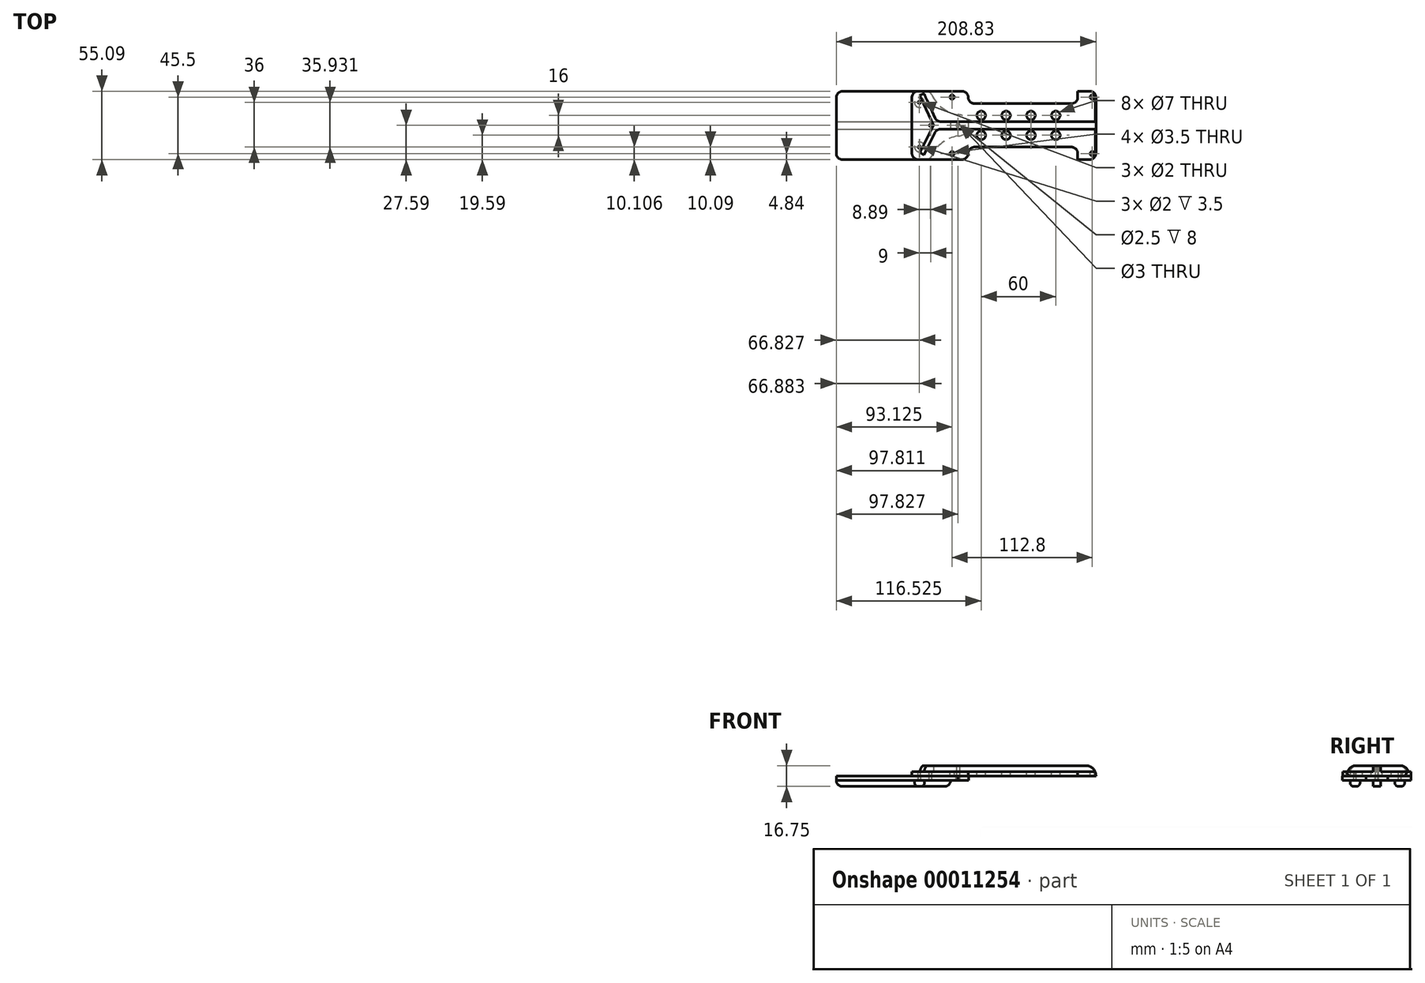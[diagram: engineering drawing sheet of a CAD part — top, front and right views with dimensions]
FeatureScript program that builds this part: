
annotation { "Feature Type Name" : "Feature", "Feature Type Description" : "" }
export const myFeature = defineFeature(function(context is Context, id is Id, definition is map)
    precondition{}
    {
        {
            var Q0;
            Q0=qCreatedBy(makeId("Front.planeOp"),FACE);
            var sketch = newSketch(context, id + "F0", { "sketchPlane" : qUnion([Q0])});
            skLineSegment(sketch, "E0.bottom", {"start": v(-74.3, 0) * mm, "end": v(73.7, 0) * mm});
            skLineSegment(sketch, "E0.top", {"start": v(-74.3, 3.25) * mm, "end": v(73.7, 3.25) * mm});
            skLineSegment(sketch, "E0.left", {"start": v(-74.3, 0) * mm, "end": v(-74.3, 3.25) * mm});
            skLineSegment(sketch, "E0.right", {"start": v(73.7, 0) * mm, "end": v(73.7, 3.25) * mm});
            skSolve(sketch);
        }
        {
            var Q0;
            Q0 = qSketchRegion(id + "F0", true);
            extrude(context, id + "F1", {"entities" : qUnion([Q0]), "endBound" : BoundingType.SYMMETRIC, "oppositeDirection" : true, "depth" : (55) * mm});
        }
        {
            var Q0;
            Q0=makeQuery(id+"F1.opExtrude","SWEPT_FACE",FACE,{"disambiguationData":[OSD([sQuery(id+"F0.wireOp",EDGE,"E0.top")])]});
            var sketch = newSketch(context, id + "F2", { "sketchPlane" : qUnion([Q0])});
            skCircle(sketch, "E1", {"center": v(70.8, 22.75) * mm, "radius": 1.75 * mm});
            skCircle(sketch, "E2", {"center": v(70.8, -22.75) * mm, "radius": 1.75 * mm});
            skCircle(sketch, "E3", {"center": v(-42, 22.75) * mm, "radius": 1.75 * mm});
            skCircle(sketch, "E4", {"center": v(-42, -22.75) * mm, "radius": 1.75 * mm});
            skLineSegment(sketch, "E5.bottom", {"start": v(-29, 27.5) * mm, "end": v(59, 27.5) * mm});
            skLineSegment(sketch, "E5.top", {"start": v(-29, 17.5) * mm, "end": v(59, 17.5) * mm});
            skLineSegment(sketch, "E5.left", {"start": v(-29, 27.5) * mm, "end": v(-29, 17.5) * mm});
            skLineSegment(sketch, "E5.right", {"start": v(59, 27.5) * mm, "end": v(59, 17.5) * mm});
            skLineSegment(sketch, "E6.bottom", {"start": v(-29, -27.5) * mm, "end": v(59, -27.5) * mm});
            skLineSegment(sketch, "E6.top", {"start": v(-29, -17.5) * mm, "end": v(59, -17.5) * mm});
            skLineSegment(sketch, "E6.left", {"start": v(-29, -27.5) * mm, "end": v(-29, -17.5) * mm});
            skLineSegment(sketch, "E6.right", {"start": v(59, -27.5) * mm, "end": v(59, -17.5) * mm});
            skCircle(sketch, "E7", {"center": v(-18.6, 8) * mm, "radius": 3.5 * mm});
            skCircle(sketch, "E8", {"center": v(1.4, 8) * mm, "radius": 3.5 * mm});
            skCircle(sketch, "E9", {"center": v(21.4, 8) * mm, "radius": 3.5 * mm});
            skCircle(sketch, "E10", {"center": v(41.4, 8) * mm, "radius": 3.5 * mm});
            skCircle(sketch, "E11", {"center": v(41.4, -8) * mm, "radius": 3.5 * mm});
            skCircle(sketch, "E12", {"center": v(21.4, -8) * mm, "radius": 3.5 * mm});
            skCircle(sketch, "E13", {"center": v(1.4, -8) * mm, "radius": 3.5 * mm});
            skCircle(sketch, "E14", {"center": v(-18.6, -8) * mm, "radius": 3.5 * mm});
            skCircle(sketch, "E15", {"center": v(-68.3, 18.5) * mm, "radius": 1 * mm});
            skCircle(sketch, "E16", {"center": v(-68.3, -17.5) * mm, "radius": 1 * mm});
            skCircle(sketch, "E17", {"center": v(-59.3, 0) * mm, "radius": 1 * mm});
            skSolve(sketch);
        }
        {
            var Q0;
            Q0 = qSketchRegion(id + "F2", true);
            extrude(context, id + "F3", {"entities" : qUnion([Q0]), "operationType" : NewBodyOperationType.REMOVE, "endBound" : BoundingType.THROUGH_ALL, "oppositeDirection" : true, "depth" : 25 * mm});
        }
        {
            var Q0;
            Q0=makeQuery(id+"F3.boolean.opBoolean","COPY",EDGE,{"derivedFrom":makeQuery(id+"F3.opExtrude","SWEPT_EDGE",EDGE,{"disambiguationData":[OSD([sQuery(id+"F0.wireOp",EDGE,"E0.top"),sQuery(id+"F2.wireOp",EDGE,"E6.bottom"),sQuery(id+"F2.wireOp",EDGE,"E6.right")])]})});
            var Q1;
            Q1=makeQuery(id+"F3.boolean.opBoolean","COPY",EDGE,{"derivedFrom":makeQuery(id+"F3.opExtrude","SWEPT_EDGE",EDGE,{"disambiguationData":[OSD([sQuery(id+"F2.wireOp",EDGE,"E6.top"),sQuery(id+"F2.wireOp",EDGE,"E6.right")])]})});
            var Q2;
            Q2=makeQuery(id+"F3.boolean.opBoolean","COPY",EDGE,{"derivedFrom":makeQuery(id+"F3.opExtrude","SWEPT_EDGE",EDGE,{"disambiguationData":[OSD([sQuery(id+"F0.wireOp",EDGE,"E0.top"),sQuery(id+"F2.wireOp",EDGE,"E6.bottom"),sQuery(id+"F2.wireOp",EDGE,"E6.left")])]})});
            var Q3;
            Q3=makeQuery(id+"F3.boolean.opBoolean","COPY",EDGE,{"derivedFrom":makeQuery(id+"F3.opExtrude","SWEPT_EDGE",EDGE,{"disambiguationData":[OSD([sQuery(id+"F0.wireOp",EDGE,"E0.top"),sQuery(id+"F2.wireOp",EDGE,"E5.bottom"),sQuery(id+"F2.wireOp",EDGE,"E5.right")])]})});
            var Q4;
            Q4=makeQuery(id+"F3.boolean.opBoolean","COPY",EDGE,{"derivedFrom":makeQuery(id+"F3.opExtrude","SWEPT_EDGE",EDGE,{"disambiguationData":[OSD([sQuery(id+"F2.wireOp",EDGE,"E6.top"),sQuery(id+"F2.wireOp",EDGE,"E6.left")])]})});
            var Q5;
            Q5=makeQuery(id+"F3.boolean.opBoolean","COPY",EDGE,{"derivedFrom":makeQuery(id+"F3.opExtrude","SWEPT_EDGE",EDGE,{"disambiguationData":[OSD([sQuery(id+"F0.wireOp",EDGE,"E0.top"),sQuery(id+"F2.wireOp",EDGE,"E5.bottom"),sQuery(id+"F2.wireOp",EDGE,"E5.left")])]})});
            var Q6;
            Q6=makeQuery(id+"F3.boolean.opBoolean","COPY",EDGE,{"derivedFrom":makeQuery(id+"F3.opExtrude","SWEPT_EDGE",EDGE,{"disambiguationData":[OSD([sQuery(id+"F2.wireOp",EDGE,"E5.top"),sQuery(id+"F2.wireOp",EDGE,"E5.left")])]})});
            var Q7;
            Q7=makeQuery(id+"F3.boolean.opBoolean","COPY",EDGE,{"derivedFrom":makeQuery(id+"F3.opExtrude","SWEPT_EDGE",EDGE,{"disambiguationData":[OSD([sQuery(id+"F2.wireOp",EDGE,"E5.top"),sQuery(id+"F2.wireOp",EDGE,"E5.right")])]})});
            var Q8;
            Q8=makeQuery(id+"F1.opExtrude","CAP_EDGE",EDGE,{"disambiguationData":[OSD([sQuery(id+"F0.wireOp",EDGE,"E0.right")])],"isStart":false});
            var Q9;
            Q9=makeQuery(id+"F1.opExtrude","CAP_EDGE",EDGE,{"disambiguationData":[OSD([sQuery(id+"F0.wireOp",EDGE,"E0.right")])],"isStart":true});
            var Q10;
            Q10=makeQuery(id+"F1.opExtrude","CAP_EDGE",EDGE,{"disambiguationData":[OSD([sQuery(id+"F0.wireOp",EDGE,"E0.left")])],"isStart":false});
            var Q11;
            Q11=makeQuery(id+"F1.opExtrude","CAP_EDGE",EDGE,{"disambiguationData":[OSD([sQuery(id+"F0.wireOp",EDGE,"E0.left")])],"isStart":true});
            fillet(context, id + "F4", {"entities" : qUnion([Q0, Q1, Q2, Q3, Q4, Q5, Q6, Q7, Q8, Q9, Q10, Q11]), "radius" : 5 * mm, "tangentPropagation" : true, "allowEdgeOverflow" : false});
        }
        {
            var Q0;
            Q0=makeQuery(id+"F1.opExtrude","SWEPT_FACE",FACE,{"disambiguationData":[OSD([sQuery(id+"F0.wireOp",EDGE,"E0.top")])]});
            var sketch = newSketch(context, id + "F5", { "sketchPlane" : qUnion([Q0])});
            skLineSegment(sketch, "E18.bottom", {"start": v(-54.3, 3) * mm, "end": v(73.7, 3) * mm});
            skLineSegment(sketch, "E18.top", {"start": v(-54.3, -3) * mm, "end": v(73.7, -3) * mm});
            skLineSegment(sketch, "E18.left", {"start": v(-54.3, 3) * mm, "end": v(-54.3, -3) * mm});
            skLineSegment(sketch, "E18.right", {"start": v(73.7, 3) * mm, "end": v(73.7, -3) * mm});
            skSolve(sketch);
        }
        {
            var Q0;
            Q0 = qSketchRegion(id + "F5", true);
            extrude(context, id + "F6", {"entities" : qUnion([Q0]), "operationType" : NewBodyOperationType.ADD, "depth" : 5 * mm});
        }
        {
            var Q0;
            Q0=qCreatedBy(makeId("Top.planeOp"),FACE);
            var sketch = newSketch(context, id + "F7", { "sketchPlane" : qUnion([Q0])});
            skLineSegment(sketch, "E19.bottom", {"start": v(-130.13, 27.41) * mm, "end": v(-59.55, 27.41) * mm});
            skLineSegment(sketch, "E19.top", {"start": v(-130.13, -27.59) * mm, "end": v(-59.56, -27.59) * mm});
            skLineSegment(sketch, "E19.left", {"start": v(-135.13, 22.41) * mm, "end": v(-135.13, -22.59) * mm});
            skPoint(sketch, "E20.visualSharp", {"position": v(-135.13, 27.41) * mm});
            skArc(sketch, "E20.filletArc", {"start": v(-130.13, 27.41) * mm, "mid": v(-133.67, 25.95) * mm, "end": v(-135.13, 22.41) * mm});
            skPoint(sketch, "E21.visualSharp", {"position": v(-135.13, -27.59) * mm});
            skArc(sketch, "E21.filletArc", {"start": v(-135.13, -22.59) * mm, "mid": v(-133.67, -26.12) * mm, "end": v(-130.13, -27.59) * mm});
            skPoint(sketch, "E22.first.point", {"position": v(-48.97, 20.64) * mm});
            skPoint(sketch, "E22.second.point", {"position": v(-62.18, 23.85) * mm});
            skPoint(sketch, "E23.first.point", {"position": v(-54.13, 12.5) * mm});
            skPoint(sketch, "E23.second.point", {"position": v(-47.93, 3.95) * mm});
            skPoint(sketch, "E24.first.point", {"position": v(-47.93, -3.95) * mm});
            skPoint(sketch, "E24.second.point", {"position": v(-54.13, -12.5) * mm});
            skPoint(sketch, "E25.orphan", {"position": v(-45.13, 27.41) * mm});
            skPoint(sketch, "E26.visualSharp", {"position": v(-52.18, -27.59) * mm});
            skPoint(sketch, "E27.visualSharp", {"position": v(-52.18, 27.41) * mm});
            skPoint(sketch, "E28.center.orphan", {"position": v(-59.31, 0) * mm});
            skPoint(sketch, "E29.center.orphan", {"position": v(-45.13, 12.5) * mm});
            skPoint(sketch, "E30.center.orphan", {"position": v(-45.13, -12.5) * mm});
            skArc(sketch, "E31", {"start": v(-45.13, -2.26) * mm, "mid": v(-45.34, -2.42) * mm, "end": v(-45.54, -2.6) * mm});
            skCircle(sketch, "E32", {"center": v(-37.3, 0) * mm, "radius": 1.5 * mm});
            skArc(sketch, "E33", {"start": v(-37.3, -8.64) * mm, "mid": v(-28.67, 0) * mm, "end": v(-37.3, 8.64) * mm});
            skArc(sketch, "E34", {"start": v(-35.36, -8.42) * mm, "mid": v(-50.38, -14.31) * mm, "end": v(-59.56, -27.59) * mm});
            skPoint(sketch, "E34.first.point", {"position": v(-37.3, -8.64) * mm});
            skPoint(sketch, "E34.third.point", {"position": v(-18.6, -12.5) * mm});
            skArc(sketch, "E35", {"start": v(-59.55, 27.41) * mm, "mid": v(-50.25, 14.27) * mm, "end": v(-35.26, 8.4) * mm});
            skPoint(sketch, "E35.first.point", {"position": v(-37.3, 8.64) * mm});
            skPoint(sketch, "E35.third.point", {"position": v(-18.6, 12.23) * mm});
            skArc(sketch, "E36.trimOffspring", {"start": v(-45.54, 2.6) * mm, "mid": v(-45.34, 2.43) * mm, "end": v(-45.13, 2.27) * mm});
            skSolve(sketch);
        }
        {
            var Q0;
            Q0 = qSketchRegion(id + "F7", true);
            extrude(context, id + "F8", {"entities" : qUnion([Q0]), "oppositeDirection" : true, "depth" : 3.5 * mm});
        }
        {
            var Q0;
            Q0=makeQuery(id+"F8.opExtrude","SWEPT_EDGE",EDGE,{"disambiguationData":[OSD([sQuery(id+"F7.wireOp",EDGE,"E19.top"),sQuery(id+"F7.wireOp",EDGE,"E31")])]});
            var Q1;
            Q1=makeQuery(id+"F8.opExtrude","SWEPT_EDGE",EDGE,{"disambiguationData":[OSD([sQuery(id+"F7.wireOp",EDGE,"E19.right"),sQuery(id+"F7.wireOp",EDGE,"E31")])]});
            var Q2;
            Q2=makeQuery(id+"F8.opExtrude","SWEPT_EDGE",EDGE,{"disambiguationData":[OSD([sQuery(id+"F7.wireOp",EDGE,"E19.right"),sQuery(id+"F7.wireOp",EDGE,"36223a7f-b2fd-4c17-a095-cdd732cdaffc")])]});
            var Q3;
            Q3=makeQuery(id+"F8.opExtrude","SWEPT_EDGE",EDGE,{"disambiguationData":[OSD([sQuery(id+"F7.wireOp",EDGE,"E19.bottom"),sQuery(id+"F7.wireOp",EDGE,"36223a7f-b2fd-4c17-a095-cdd732cdaffc")])]});
            fillet(context, id + "F9", {"entities" : qUnion([Q0, Q1, Q2, Q3]), "radius" : 5 * mm, "tangentPropagation" : true, "allowEdgeOverflow" : false});
        }
        {
            var Q0;
            Q0=makeQuery(id+"F8.opExtrude","CAP_FACE",FACE,{"disambiguationData":[OSD([sQuery(id+"F7.wireOp",EDGE,"E19.bottom"),sQuery(id+"F7.wireOp",EDGE,"E19.top"),sQuery(id+"F7.wireOp",EDGE,"E19.left"),sQuery(id+"F7.wireOp",EDGE,"E19.right"),sQuery(id+"F7.wireOp",EDGE,"E20.filletArc"),sQuery(id+"F7.wireOp",EDGE,"E21.filletArc"),sQuery(id+"F7.wireOp",EDGE,"E31"),sQuery(id+"F7.wireOp",EDGE,"36223a7f-b2fd-4c17-a095-cdd732cdaffc")])],"isStart":true});
            var sketch = newSketch(context, id + "F10", { "sketchPlane" : qUnion([Q0])});
            skCircle(sketch, "E37", {"center": v(-68.25, 18.45) * mm, "radius": 1 * mm});
            skCircle(sketch, "E38", {"center": v(-59.36, 0) * mm, "radius": 1 * mm});
            skCircle(sketch, "E39", {"center": v(-68.17, -17.48) * mm, "radius": 1 * mm});
            skSolve(sketch);
        }
        {
            var Q0;
            Q0 = qSketchRegion(id + "F10", true);
            extrude(context, id + "F11", {"entities" : qUnion([Q0]), "operationType" : NewBodyOperationType.REMOVE, "oppositeDirection" : true, "depth" : 8 * mm});
        }
        {
            var Q0;
            Q0=makeQuery(id+"F8.opExtrude","CAP_FACE",FACE,{"disambiguationData":[OSD([sQuery(id+"F7.wireOp",EDGE,"E19.bottom"),sQuery(id+"F7.wireOp",EDGE,"E19.top"),sQuery(id+"F7.wireOp",EDGE,"E19.left"),sQuery(id+"F7.wireOp",EDGE,"E19.right"),sQuery(id+"F7.wireOp",EDGE,"E20.filletArc"),sQuery(id+"F7.wireOp",EDGE,"E21.filletArc"),sQuery(id+"F7.wireOp",EDGE,"E31"),sQuery(id+"F7.wireOp",EDGE,"36223a7f-b2fd-4c17-a095-cdd732cdaffc")])],"isStart":false});
            var sketch = newSketch(context, id + "F12", { "sketchPlane" : qUnion([Q0])});
            skLineSegment(sketch, "E40.bottom", {"start": v(-135.13, 3) * mm, "end": v(-43.13, 3) * mm});
            skLineSegment(sketch, "E40.top", {"start": v(-135.13, -3) * mm, "end": v(-43.13, -3) * mm});
            skLineSegment(sketch, "E40.left", {"start": v(-135.13, 3) * mm, "end": v(-135.13, -3) * mm});
            skLineSegment(sketch, "E40.right", {"start": v(-43.13, 3) * mm, "end": v(-43.13, -3) * mm});
            skSolve(sketch);
        }
        {
            var Q0;
            Q0 = qSketchRegion(id + "F12", true);
            extrude(context, id + "F13", {"entities" : qUnion([Q0]), "operationType" : NewBodyOperationType.ADD, "depth" : 5 * mm});
        }
        {
            var Q0;
            Q0=makeQuery(id+"F13.opExtrude","CAP_EDGE",EDGE,{"disambiguationData":[OSD([sQuery(id+"F12.wireOp",EDGE,"E40.left")])],"isStart":false});
            var Q1;
            Q1=makeQuery(id+"F13.opExtrude","CAP_EDGE",EDGE,{"disambiguationData":[OSD([sQuery(id+"F12.wireOp",EDGE,"E40.right")])],"isStart":false});
            fillet(context, id + "F14", {"entities" : qUnion([Q0, Q1]), "radius" : 5 * mm, "tangentPropagation" : true, "allowEdgeOverflow" : false});
        }
        {
            var Q0;
            Q0=makeQuery(id+"F8.opExtrude","CAP_FACE",FACE,{"disambiguationData":[OSD([sQuery(id+"F7.wireOp",EDGE,"E19.bottom"),sQuery(id+"F7.wireOp",EDGE,"E19.top"),sQuery(id+"F7.wireOp",EDGE,"E19.left"),sQuery(id+"F7.wireOp",EDGE,"E19.right"),sQuery(id+"F7.wireOp",EDGE,"E20.filletArc"),sQuery(id+"F7.wireOp",EDGE,"E21.filletArc"),sQuery(id+"F7.wireOp",EDGE,"E31"),sQuery(id+"F7.wireOp",EDGE,"36223a7f-b2fd-4c17-a095-cdd732cdaffc")])],"isStart":false});
            var sketch = newSketch(context, id + "F15", { "sketchPlane" : qUnion([Q0])});
            skCircle(sketch, "E41", {"center": v(-68.17, 17.48) * mm, "radius": 4 * mm});
            skCircle(sketch, "E42", {"center": v(-68.25, -18.45) * mm, "radius": 4 * mm});
            skSolve(sketch);
        }
        {
            var Q0;
            Q0 = qSketchRegion(id + "F15", true);
            extrude(context, id + "F16", {"entities" : qUnion([Q0]), "operationType" : NewBodyOperationType.ADD, "depth" : 5 * mm});
        }
        {
            var Q0;
            Q0=makeQuery(id+"F16.opExtrude","CAP_EDGE",EDGE,{"disambiguationData":[OSD([sQuery(id+"F15.wireOp",EDGE,"E41")])],"isStart":false});
            var Q1;
            Q1=makeQuery(id+"F16.opExtrude","CAP_EDGE",EDGE,{"disambiguationData":[OSD([sQuery(id+"F15.wireOp",EDGE,"E42")])],"isStart":false});
            fillet(context, id + "F17", {"entities" : qUnion([Q0, Q1]), "radius" : 3 * mm, "tangentPropagation" : true, "allowEdgeOverflow" : false});
        }
        {
            var Q0;
            Q0=makeQuery(id+"F1.opExtrude","SWEPT_FACE",FACE,{"disambiguationData":[OSD([sQuery(id+"F0.wireOp",EDGE,"E0.top")])]});
            var sketch = newSketch(context, id + "F18", { "sketchPlane" : qUnion([Q0])});
            skLineSegment(sketch, "E43", {"start": v(-54.3, 3) * mm, "end": v(-64.62, 25.6) * mm});
            skLineSegment(sketch, "E44", {"start": v(-64.62, 25.6) * mm, "end": v(-67.96, 24.08) * mm});
            skLineSegment(sketch, "E45", {"start": v(-67.96, 24.08) * mm, "end": v(-56.97, 0) * mm});
            skLineSegment(sketch, "E46", {"start": v(-56.97, 0) * mm, "end": v(-67.96, -21.93) * mm});
            skLineSegment(sketch, "E47", {"start": v(-67.96, -21.93) * mm, "end": v(-64.62, -23.6) * mm});
            skLineSegment(sketch, "E48", {"start": v(-64.62, -23.6) * mm, "end": v(-54.3, -3) * mm});
            skLineSegment(sketch, "E49", {"start": v(-54.3, -3) * mm, "end": v(-54.3, 3) * mm});
            skSolve(sketch);
        }
        {
            var Q0;
            Q0 = qSketchRegion(id + "F18", true);
            extrude(context, id + "F19", {"entities" : qUnion([Q0]), "operationType" : NewBodyOperationType.ADD, "depth" : 5 * mm});
        }
        {
            var Q0;
            Q0=makeQuery(id+"F19.opExtrude","CAP_EDGE",EDGE,{"disambiguationData":[OSD([sQuery(id+"F18.wireOp",EDGE,"E44")])],"isStart":false});
            var Q1;
            Q1=makeQuery(id+"F19.opExtrude","CAP_EDGE",EDGE,{"disambiguationData":[OSD([sQuery(id+"F18.wireOp",EDGE,"E47")])],"isStart":false});
            var Q2;
            Q2=makeQuery(id+"F6.opExtrude","CAP_EDGE",EDGE,{"disambiguationData":[OSD([sQuery(id+"F5.wireOp",EDGE,"E18.right")])],"isStart":false});
            fillet(context, id + "F20", {"entities" : qUnion([Q0, Q1, Q2]), "radius" : 8 * mm, "tangentPropagation" : true, "allowEdgeOverflow" : false});
        }
        {
            var Q0;
            {var subQ0=sQuery(id+"F5.wireOp",EDGE,"E18.top");Q0=makeQuery(id+"F19.boolean.opBoolean","MERGE",EDGE,{"derivedFrom":[makeQuery(id+"F6.opExtrude","SWEPT_EDGE",EDGE,{"disambiguationData":[OSD([subQ0,sQuery(id+"F5.wireOp",EDGE,"E18.left")])]}),makeQuery(id+"F19.opExtrude","SWEPT_EDGE",EDGE,{"disambiguationData":[OSD([subQ0,sQuery(id+"F18.wireOp",EDGE,"E48"),sQuery(id+"F18.wireOp",EDGE,"E49")])]})]});}
            var Q1;
            {var subQ0=sQuery(id+"F5.wireOp",EDGE,"E18.bottom");Q1=makeQuery(id+"F19.boolean.opBoolean","MERGE",EDGE,{"derivedFrom":[makeQuery(id+"F6.opExtrude","SWEPT_EDGE",EDGE,{"disambiguationData":[OSD([subQ0,sQuery(id+"F5.wireOp",EDGE,"E18.left")])]}),makeQuery(id+"F19.opExtrude","SWEPT_EDGE",EDGE,{"disambiguationData":[OSD([subQ0,sQuery(id+"F18.wireOp",EDGE,"E43"),sQuery(id+"F18.wireOp",EDGE,"E49")])]})]});}
            fillet(context, id + "F21", {"entities" : qUnion([Q0, Q1]), "radius" : 5 * mm, "tangentPropagation" : true, "allowEdgeOverflow" : false});
        }
        {
            var Q0;
            Q0=makeQuery(id+"F1.opExtrude","SWEPT_FACE",FACE,{"disambiguationData":[OSD([sQuery(id+"F0.wireOp",EDGE,"E0.bottom")])]});
            var sketch = newSketch(context, id + "F22", { "sketchPlane" : qUnion([Q0])});
            skCircle(sketch, "E50", {"center": v(-37.32, 0) * mm, "radius": 1.25 * mm});
            skSolve(sketch);
        }
        {
            var Q0;
            Q0 = qSketchRegion(id + "F22", true);
            extrude(context, id + "F23", {"entities" : qUnion([Q0]), "operationType" : NewBodyOperationType.REMOVE, "oppositeDirection" : true, "depth" : 8 * mm});
        }
    });
